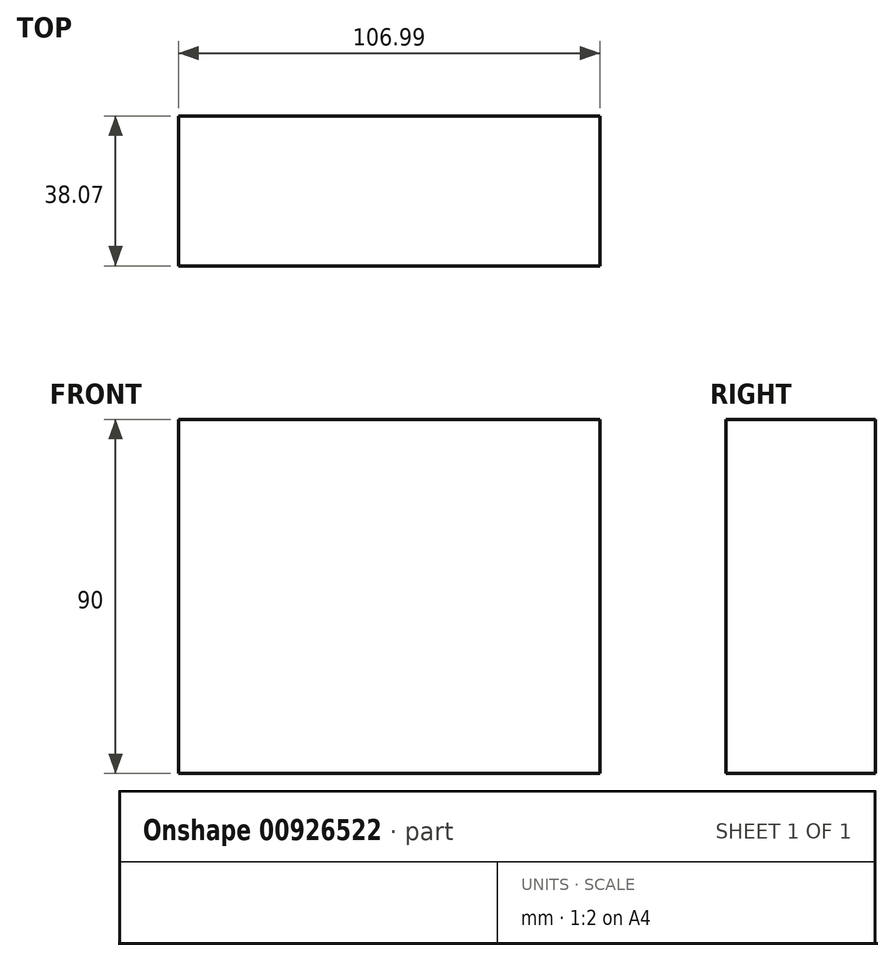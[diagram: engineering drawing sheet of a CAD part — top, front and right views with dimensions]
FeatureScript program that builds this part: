
annotation { "Feature Type Name" : "Feature", "Feature Type Description" : "" }
export const myFeature = defineFeature(function(context is Context, id is Id, definition is map)
    precondition{}
    {
        {
            var Q0;
            Q0=qCreatedBy(makeId("Top.planeOp"),FACE);
            var sketch = newSketch(context, id + "F0", { "sketchPlane" : qUnion([Q0])});
            skLineSegment(sketch, "E0.bottom", {"start": v(-31.68, 16.56) * mm, "end": v(75.31, 16.56) * mm});
            skLineSegment(sketch, "E0.top", {"start": v(-31.68, -21.51) * mm, "end": v(75.31, -21.51) * mm});
            skLineSegment(sketch, "E0.left", {"start": v(-31.68, 16.56) * mm, "end": v(-31.68, -21.51) * mm});
            skLineSegment(sketch, "E0.right", {"start": v(75.31, 16.56) * mm, "end": v(75.31, -21.51) * mm});
            skSolve(sketch);
        }
        {
            var Q0;
            Q0=makeQuery(id+"F0.imprint","IMPRINT",FACE,{"disambiguationData":[TD([[makeQuery(id+"F0.imprint","IMPRINT",EDGE,{"derivedFrom":sQuery(id+"F0.wireOp",EDGE,"E0.bottom")}),-1.0]])]});
            extrude(context, id + "F1", {"entities" : qUnion([Q0]), "depth" : 90 * mm, "offsetDistance" : 25 * mm});
        }
    });
